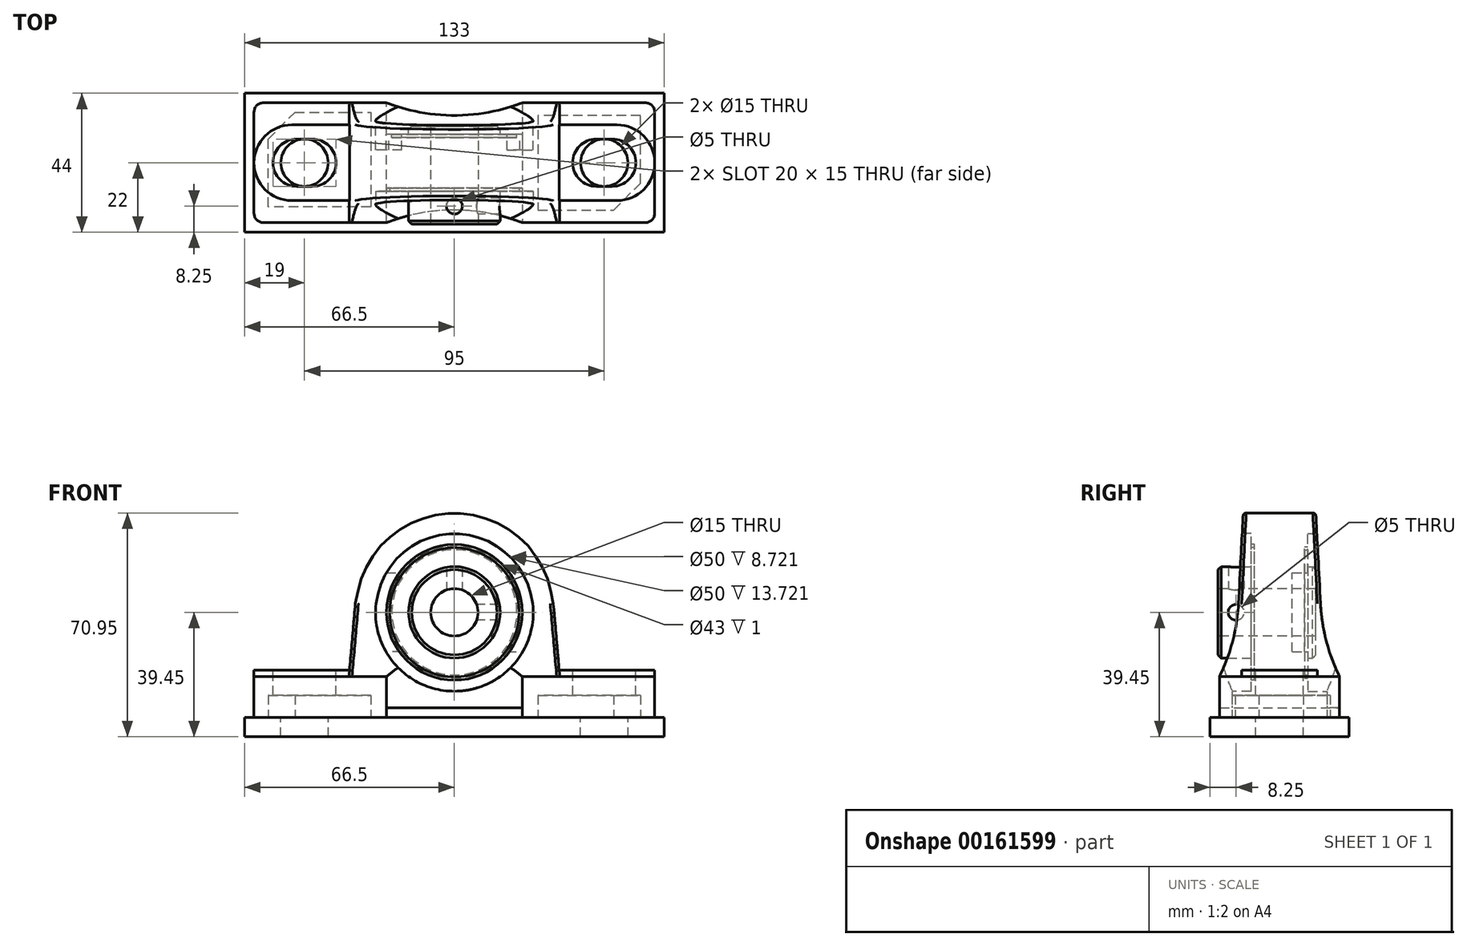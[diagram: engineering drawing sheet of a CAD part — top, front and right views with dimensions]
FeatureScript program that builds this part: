
annotation { "Feature Type Name" : "Feature", "Feature Type Description" : "" }
export const myFeature = defineFeature(function(context is Context, id is Id, definition is map)
    precondition{}
    {
        {
            var Q0;
            Q0=qCreatedBy(makeId("Front.planeOp"),FACE);
            var sketch = newSketch(context, id + "F0", { "sketchPlane" : qUnion([Q0])});
            skLineSegment(sketch, "E0", {"start": v(-63.5, 0) * mm, "end": v(0, 0) * mm});
            skLineSegment(sketch, "E1", {"start": v(-63.5, 0) * mm, "end": v(-63.5, 13) * mm});
            skLineSegment(sketch, "E2", {"start": v(-63.5, 13) * mm, "end": v(-33.4, 13) * mm});
            skCircle(sketch, "E3", {"center": v(0, 33.3) * mm, "radius": 31.5 * mm});
            skLineSegment(sketch, "E4", {"start": v(-31.38, 36.05) * mm, "end": v(-33.4, 13) * mm});
            skPoint(sketch, "E5", {"position": v(0, 64.8) * mm});
            skLineSegment(sketch, "E6.MirrorCS", {"start": v(63.5, 0) * mm, "end": v(0, 0) * mm});
            skLineSegment(sketch, "E7.MirrorCS", {"start": v(63.5, 0) * mm, "end": v(63.5, 13) * mm});
            skLineSegment(sketch, "E8.MirrorCS", {"start": v(63.5, 13) * mm, "end": v(33.4, 13) * mm});
            skLineSegment(sketch, "E9.MirrorCS", {"start": v(31.38, 36.05) * mm, "end": v(33.4, 13) * mm});
            skSolve(sketch);
        }
        {
            var Q0;
            Q0 = qSketchRegion(id + "F0", true);
            extrude(context, id + "F1", {"entities" : qUnion([Q0]), "endBound" : BoundingType.SYMMETRIC, "depth" : 38 * mm});
        }
        {
            var Q0;
            Q0=makeQuery(id+"F1.opExtrude","SWEPT_FACE",FACE,{"disambiguationData":[OSD([sQuery(id+"F0.wireOp",EDGE,"E7.MirrorCS")])]});
            var sketch = newSketch(context, id + "F2", { "sketchPlane" : qUnion([Q0])});
            skLineSegment(sketch, "E10", {"start": v(-19, 64.8) * mm, "end": v(-11.5, 64.8) * mm});
            skLineSegment(sketch, "E11", {"start": v(-11.5, 64.8) * mm, "end": v(-13, 36.05) * mm});
            skArc(sketch, "E12", {"start": v(-13, 36.05) * mm, "mid": v(-14.83, 24.22) * mm, "end": v(-19, 13) * mm});
            skLineSegment(sketch, "E13", {"start": v(-19, 13) * mm, "end": v(-19, 64.8) * mm});
            skLineSegment(sketch, "E14.MirrorCS", {"start": v(19, 64.8) * mm, "end": v(11.5, 64.8) * mm});
            skLineSegment(sketch, "E15.MirrorCS", {"start": v(11.5, 64.8) * mm, "end": v(13, 36.05) * mm});
            skArc(sketch, "E16.MirrorCS", {"start": v(13, 36.05) * mm, "mid": v(14.83, 24.22) * mm, "end": v(19, 13) * mm});
            skLineSegment(sketch, "E17.MirrorCS", {"start": v(19, 13) * mm, "end": v(19, 64.8) * mm});
            skSolve(sketch);
        }
        {
            var Q0;
            Q0 = qSketchRegion(id + "F2", true);
            var Q1;
            Q1=makeQuery(id+"F1.opExtrude","SWEPT_FACE",FACE,{"disambiguationData":[OSD([sQuery(id+"F0.wireOp",EDGE,"E1")])]});
            extrude(context, id + "F3", {"entities" : qUnion([Q0]), "operationType" : NewBodyOperationType.REMOVE, "endBound" : BoundingType.UP_TO_SURFACE, "oppositeDirection" : true, "endBoundEntityFace" : qUnion([Q1]), "depth" : 106 * mm});
        }
        {
            var Q0;
            Q0=makeQuery(id+"F1.opExtrude","SWEPT_FACE",FACE,{"disambiguationData":[OSD([sQuery(id+"F0.wireOp",EDGE,"E0"),sQuery(id+"F0.wireOp",EDGE,"E6.MirrorCS")])]});
            var sketch = newSketch(context, id + "F4", { "sketchPlane" : qUnion([Q0])});
            skArc(sketch, "E18", {"start": v(-21.5, 19) * mm, "mid": v(0, 15) * mm, "end": v(21.5, 19) * mm});
            skPoint(sketch, "E19", {"position": v(0, 15) * mm});
            skLineSegment(sketch, "E20", {"start": v(-21.5, 19) * mm, "end": v(21.5, 19) * mm});
            skArc(sketch, "E21.MirrorCS", {"start": v(-21.5, -19) * mm, "mid": v(0, -15) * mm, "end": v(21.5, -19) * mm});
            skLineSegment(sketch, "E22.MirrorCS", {"start": v(-21.5, -19) * mm, "end": v(21.5, -19) * mm});
            skPoint(sketch, "E23.MirrorP", {"position": v(0, -15) * mm});
            skSolve(sketch);
        }
        {
            var Q0;
            Q0 = qSketchRegion(id + "F4", true);
            extrude(context, id + "F5", {"entities" : qUnion([Q0]), "operationType" : NewBodyOperationType.REMOVE, "endBound" : BoundingType.UP_TO_NEXT, "oppositeDirection" : true, "depth" : 25 * mm});
        }
        {
            var Q0;
            {var subQ0=sQuery(id+"F0.wireOp",EDGE,"E4");var subQ1=sQuery(id+"F0.wireOp",EDGE,"E2");var subQ2=sQuery(id+"F0.wireOp",EDGE,"E1");var subQ3=sQuery(id+"F0.wireOp",EDGE,"E6.MirrorCS");var subQ4=sQuery(id+"F0.wireOp",EDGE,"E0");Q0=makeQuery(id+"F5.boolean.opBoolean","SPLIT",FACE,{"disambiguationData":[TD([makeQuery(id+"F1.opExtrude","SWEPT_FACE",FACE,{"disambiguationData":[OSD([subQ2])]})])],"derivedFrom":makeQuery(id+"F1.opExtrude","CAP_FACE",FACE,{"disambiguationData":[OSD([subQ4,subQ2,subQ1,sQuery(id+"F0.wireOp",EDGE,"E3"),subQ0,subQ3,sQuery(id+"F0.wireOp",EDGE,"E7.MirrorCS"),sQuery(id+"F0.wireOp",EDGE,"E8.MirrorCS"),sQuery(id+"F0.wireOp",EDGE,"E9.MirrorCS")])],"isStart":false})});}
            var sketch = newSketch(context, id + "F6", { "sketchPlane" : qUnion([Q0])});
            skCircle(sketch, "E24", {"center": v(0, 33.3) * mm, "radius": 25 * mm});
            skSolve(sketch);
        }
        {
            var Q0;
            Q0 = qSketchRegion(id + "F6", true);
            extrude(context, id + "F7", {"entities" : qUnion([Q0]), "operationType" : NewBodyOperationType.REMOVE, "oppositeDirection" : true, "depth" : 10 * mm});
        }
        {
            var Q0;
            {var subQ0=sQuery(id+"F0.wireOp",EDGE,"E7.MirrorCS");var subQ1=sQuery(id+"F0.wireOp",EDGE,"E9.MirrorCS");var subQ2=sQuery(id+"F0.wireOp",EDGE,"E8.MirrorCS");var subQ3=sQuery(id+"F0.wireOp",EDGE,"E6.MirrorCS");var subQ4=sQuery(id+"F0.wireOp",EDGE,"E0");Q0=makeQuery(id+"F5.boolean.opBoolean","SPLIT",FACE,{"disambiguationData":[TD([makeQuery(id+"F1.opExtrude","SWEPT_FACE",FACE,{"disambiguationData":[OSD([subQ0])]})])],"derivedFrom":makeQuery(id+"F1.opExtrude","CAP_FACE",FACE,{"disambiguationData":[OSD([subQ4,sQuery(id+"F0.wireOp",EDGE,"E1"),sQuery(id+"F0.wireOp",EDGE,"E2"),sQuery(id+"F0.wireOp",EDGE,"E3"),sQuery(id+"F0.wireOp",EDGE,"E4"),subQ3,subQ0,subQ2,subQ1])],"isStart":true})});}
            var sketch = newSketch(context, id + "F8", { "sketchPlane" : qUnion([Q0])});
            skCircle(sketch, "E25", {"center": v(0, 33.3) * mm, "radius": 25 * mm});
            skSolve(sketch);
        }
        {
            var Q0;
            Q0 = qSketchRegion(id + "F8", true);
            extrude(context, id + "F9", {"entities" : qUnion([Q0]), "operationType" : NewBodyOperationType.REMOVE, "oppositeDirection" : true, "depth" : 10 * mm});
        }
        {
            var Q0;
            Q0=makeQuery(id+"F7.boolean.opBoolean","COPY",FACE,{"derivedFrom":makeQuery(id+"F7.opExtrude","CAP_FACE",FACE,{"disambiguationData":[OSD([sQuery(id+"F6.wireOp",EDGE,"E24")])],"isStart":false})});
            var sketch = newSketch(context, id + "F10", { "sketchPlane" : qUnion([Q0])});
            skCircle(sketch, "E26", {"center": v(0, 33.3) * mm, "radius": 21.5 * mm});
            skCircle(sketch, "E27", {"center": v(0, 33.3) * mm, "radius": 20.5 * mm});
            skSolve(sketch);
        }
        {
            var Q0;
            Q0 = qSketchRegion(id + "F10", true);
            extrude(context, id + "F11", {"entities" : qUnion([Q0]), "operationType" : NewBodyOperationType.REMOVE, "oppositeDirection" : true, "depth" : 1 * mm});
        }
        {
            var Q0;
            Q0=qCreatedBy(makeId("Front.planeOp"),FACE);
            cPlane(context, id + "F12", {"entities" : qUnion([Q0]), "cplaneType" : CPlaneType.OFFSET, "offset" : 4 * mm, "width" : 150 * mm, "height" : 150 * mm});
        }
        {
            var Q0;
            Q0=qCreatedBy(id+"F12.planeOp",FACE);
            var sketch = newSketch(context, id + "F13", { "sketchPlane" : qUnion([Q0])});
            skCircle(sketch, "E28", {"center": v(0, 33.3) * mm, "radius": 14.5 * mm});
            skSolve(sketch);
        }
        {
            var Q0;
            Q0 = qSketchRegion(id + "F13", true);
            extrude(context, id + "F14", {"entities" : qUnion([Q0]), "operationType" : NewBodyOperationType.ADD, "endBound" : BoundingType.SYMMETRIC, "depth" : 31 * mm});
        }
        {
            var Q0;
            Q0=makeQuery(id+"F14.opExtrude","CAP_FACE",FACE,{"disambiguationData":[OSD([sQuery(id+"F13.wireOp",EDGE,"E28")])],"isStart":false});
            var sketch = newSketch(context, id + "F15", { "sketchPlane" : qUnion([Q0])});
            skCircle(sketch, "E29", {"center": v(0, 33.3) * mm, "radius": 7.5 * mm});
            skSolve(sketch);
        }
        {
            var Q0;
            Q0 = qSketchRegion(id + "F15", true);
            extrude(context, id + "F16", {"entities" : qUnion([Q0]), "operationType" : NewBodyOperationType.REMOVE, "endBound" : BoundingType.UP_TO_NEXT, "oppositeDirection" : true, "depth" : 25 * mm});
        }
        {
            var Q0;
            Q0=makeQuery(id+"F9.boolean.opBoolean","COPY",FACE,{"derivedFrom":makeQuery(id+"F9.opExtrude","CAP_FACE",FACE,{"disambiguationData":[OSD([sQuery(id+"F8.wireOp",EDGE,"E25")])],"isStart":false})});
            var sketch = newSketch(context, id + "F17", { "sketchPlane" : qUnion([Q0])});
            skArc(sketch, "E30", {"start": v(-21.65, 45.8) * mm, "mid": v(-25, 33.3) * mm, "end": v(-21.65, 20.8) * mm});
            skArc(sketch, "E31", {"start": v(-16.65, 45.8) * mm, "mid": v(-20.82, 33.3) * mm, "end": v(-16.65, 20.8) * mm});
            skLineSegment(sketch, "E32", {"start": v(-21.65, 45.8) * mm, "end": v(-16.65, 45.8) * mm});
            skLineSegment(sketch, "E33", {"start": v(-16.65, 20.8) * mm, "end": v(-21.65, 20.8) * mm});
            skPoint(sketch, "E34", {"position": v(-20.82, 33.3) * mm});
            skArc(sketch, "E35.MirrorCS", {"start": v(16.65, 45.8) * mm, "mid": v(20.82, 33.3) * mm, "end": v(16.65, 20.8) * mm});
            skArc(sketch, "E36.MirrorCS", {"start": v(21.65, 45.8) * mm, "mid": v(25, 33.3) * mm, "end": v(21.65, 20.8) * mm});
            skPoint(sketch, "E37.MirrorP", {"position": v(20.82, 33.3) * mm});
            skLineSegment(sketch, "E38.MirrorCS", {"start": v(16.65, 20.8) * mm, "end": v(21.65, 20.8) * mm});
            skLineSegment(sketch, "E39.MirrorCS", {"start": v(21.65, 45.8) * mm, "end": v(16.65, 45.8) * mm});
            skSolve(sketch);
        }
        {
            var Q0;
            Q0 = qSketchRegion(id + "F17", true);
            extrude(context, id + "F18", {"entities" : qUnion([Q0]), "operationType" : NewBodyOperationType.REMOVE, "oppositeDirection" : true, "depth" : 5 * mm});
        }
        {
            var Q0;
            Q0=makeQuery(id+"F9.boolean.opBoolean","COPY",FACE,{"derivedFrom":makeQuery(id+"F9.opExtrude","CAP_FACE",FACE,{"disambiguationData":[OSD([sQuery(id+"F8.wireOp",EDGE,"E25")])],"isStart":false})});
            var sketch = newSketch(context, id + "F19", { "sketchPlane" : qUnion([Q0])});
            skCircle(sketch, "E40", {"center": v(0, 33.3) * mm, "radius": 20.82 * mm});
            skCircle(sketch, "E41", {"center": v(0, 33.3) * mm, "radius": 19.82 * mm});
            skSolve(sketch);
        }
        {
            var Q0;
            Q0 = qSketchRegion(id + "F19", true);
            extrude(context, id + "F20", {"entities" : qUnion([Q0]), "operationType" : NewBodyOperationType.REMOVE, "oppositeDirection" : true, "depth" : 1 * mm});
        }
        {
            var Q0;
            Q0=makeQuery(id+"F1.opExtrude","SWEPT_FACE",FACE,{"disambiguationData":[OSD([sQuery(id+"F0.wireOp",EDGE,"E0"),sQuery(id+"F0.wireOp",EDGE,"E6.MirrorCS")])]});
            var sketch = newSketch(context, id + "F21", { "sketchPlane" : qUnion([Q0])});
            skLineSegment(sketch, "E42", {"start": v(-21.5, 19) * mm, "end": v(-21.5, -19) * mm});
            skLineSegment(sketch, "E43", {"start": v(-21.5, -19) * mm, "end": v(21.5, -19) * mm});
            skLineSegment(sketch, "E44", {"start": v(21.5, -19) * mm, "end": v(21.5, 19) * mm});
            skLineSegment(sketch, "E45", {"start": v(21.5, 19) * mm, "end": v(-21.5, 19) * mm});
            skSolve(sketch);
        }
        {
            var Q0;
            Q0 = qSketchRegion(id + "F21", true);
            extrude(context, id + "F22", {"entities" : qUnion([Q0]), "operationType" : NewBodyOperationType.REMOVE, "oppositeDirection" : true, "depth" : 3 * mm});
        }
        {
            var Q0;
            {var subQ3=sQuery(id+"F0.wireOp",EDGE,"E6.MirrorCS");var subQ7=sQuery(id+"F0.wireOp",EDGE,"E1");var subQ8=sQuery(id+"F0.wireOp",EDGE,"E0");Q0=makeQuery(id+"F22.boolean.opBoolean","SPLIT",FACE,{"disambiguationData":[TD([makeQuery(id+"F1.opExtrude","SWEPT_FACE",FACE,{"disambiguationData":[OSD([subQ7])]})])],"derivedFrom":makeQuery(id+"F1.opExtrude","SWEPT_FACE",FACE,{"disambiguationData":[OSD([subQ8,subQ3])]})});}
            var sketch = newSketch(context, id + "F23", { "sketchPlane" : qUnion([Q0])});
            skLineSegment(sketch, "E46", {"start": v(26.5, 15) * mm, "end": v(50.51, 15) * mm});
            skLineSegment(sketch, "E47", {"start": v(50.51, 15) * mm, "end": v(59, 6.51) * mm});
            skLineSegment(sketch, "E48", {"start": v(59, 6.51) * mm, "end": v(59, -15) * mm});
            skLineSegment(sketch, "E49", {"start": v(59, -15) * mm, "end": v(26.5, -15) * mm});
            skLineSegment(sketch, "E50", {"start": v(26.5, -15) * mm, "end": v(26.5, 15) * mm});
            skPoint(sketch, "E51", {"position": v(26.5, 0) * mm});
            skLineSegment(sketch, "E52", {"start": v(-59, -7.51) * mm, "end": v(-50.51, -16) * mm});
            skLineSegment(sketch, "E53", {"start": v(-50.51, -16) * mm, "end": v(-26.5, -16) * mm});
            skLineSegment(sketch, "E54", {"start": v(-26.5, -16) * mm, "end": v(-26.5, 14) * mm});
            skLineSegment(sketch, "E55", {"start": v(-26.5, 14) * mm, "end": v(-59, 14) * mm});
            skLineSegment(sketch, "E56", {"start": v(-59, 14) * mm, "end": v(-59, -7.51) * mm});
            skSolve(sketch);
        }
        {
            var Q0;
            Q0 = qSketchRegion(id + "F23", true);
            extrude(context, id + "F24", {"entities" : qUnion([Q0]), "operationType" : NewBodyOperationType.REMOVE, "oppositeDirection" : true, "depth" : 7 * mm});
        }
        {
            var Q0;
            Q0=makeQuery(id+"F1.opExtrude","SWEPT_FACE",FACE,{"disambiguationData":[OSD([sQuery(id+"F0.wireOp",EDGE,"E2")])]});
            var sketch = newSketch(context, id + "F25", { "sketchPlane" : qUnion([Q0])});
            skLineSegment(sketch, "E57", {"start": v(31.38, 12) * mm, "end": v(51.5, 12) * mm});
            skLineSegment(sketch, "E58", {"start": v(31.38, 12) * mm, "end": v(31.38, -12) * mm});
            skLineSegment(sketch, "E59", {"start": v(31.38, -12) * mm, "end": v(51.5, -12) * mm});
            skArc(sketch, "E60", {"start": v(51.5, 12) * mm, "mid": v(63.5, 0) * mm, "end": v(51.5, -12) * mm});
            skArc(sketch, "E61.MirrorCS", {"start": v(-51.5, 12) * mm, "mid": v(-63.5, 0) * mm, "end": v(-51.5, -12) * mm});
            skLineSegment(sketch, "E62.MirrorCS", {"start": v(-31.38, -12) * mm, "end": v(-51.5, -12) * mm});
            skLineSegment(sketch, "E63.MirrorCS", {"start": v(-31.38, 12) * mm, "end": v(-31.38, -12) * mm});
            skLineSegment(sketch, "E64.MirrorCS", {"start": v(-31.38, 12) * mm, "end": v(-51.5, 12) * mm});
            skSolve(sketch);
        }
        {
            var Q0;
            Q0 = qSketchRegion(id + "F25", true);
            extrude(context, id + "F26", {"entities" : qUnion([Q0]), "operationType" : NewBodyOperationType.ADD, "depth" : 2 * mm});
        }
        {
            var Q0;
            Q0=makeQuery(id+"F26.opExtrude","CAP_FACE",FACE,{"disambiguationData":[OSD([sQuery(id+"F25.wireOp",EDGE,"E61.MirrorCS"),sQuery(id+"F25.wireOp",EDGE,"E62.MirrorCS"),sQuery(id+"F25.wireOp",EDGE,"E63.MirrorCS"),sQuery(id+"F25.wireOp",EDGE,"E64.MirrorCS")])],"isStart":false});
            var sketch = newSketch(context, id + "F27", { "sketchPlane" : qUnion([Q0])});
            skLineSegment(sketch, "E65.bottom", {"start": v(-50, 7.5) * mm, "end": v(-45, 7.5) * mm});
            skLineSegment(sketch, "E65.top", {"start": v(-50, -7.5) * mm, "end": v(-45, -7.5) * mm});
            skLineSegment(sketch, "E65.left", {"start": v(-50, 7.5) * mm, "end": v(-50, -7.5) * mm, "construction": true});
            skLineSegment(sketch, "E65.right", {"start": v(-45, 7.5) * mm, "end": v(-45, -7.5) * mm, "construction": true});
            skPoint(sketch, "E65.middle", {"position": v(-47.5, 0) * mm});
            skArc(sketch, "E66", {"start": v(-50, 7.5) * mm, "mid": v(-57.5, 0) * mm, "end": v(-50, -7.5) * mm});
            skArc(sketch, "E67", {"start": v(-45, 7.5) * mm, "mid": v(-37.5, 0) * mm, "end": v(-45, -7.5) * mm});
            skPoint(sketch, "E68", {"position": v(-37.5, 0) * mm});
            skPoint(sketch, "E69", {"position": v(-57.5, 0) * mm});
            skPoint(sketch, "E70.MirrorP", {"position": v(47.5, 0) * mm});
            skPoint(sketch, "E71.MirrorP", {"position": v(37.5, 0) * mm});
            skPoint(sketch, "E72.MirrorP", {"position": v(57.5, 0) * mm});
            skLineSegment(sketch, "E73.MirrorCS", {"start": v(50, 7.5) * mm, "end": v(45, 7.5) * mm});
            skLineSegment(sketch, "E74.MirrorCS", {"start": v(50, -7.5) * mm, "end": v(45, -7.5) * mm});
            skLineSegment(sketch, "E75.MirrorCS", {"start": v(50, 7.5) * mm, "end": v(50, -7.5) * mm, "construction": true});
            skLineSegment(sketch, "E76.MirrorCS", {"start": v(45, 7.5) * mm, "end": v(45, -7.5) * mm, "construction": true});
            skArc(sketch, "E77.MirrorCS", {"start": v(50, 7.5) * mm, "mid": v(57.5, 0) * mm, "end": v(50, -7.5) * mm});
            skArc(sketch, "E78.MirrorCS", {"start": v(45, 7.5) * mm, "mid": v(37.5, 0) * mm, "end": v(45, -7.5) * mm});
            skSolve(sketch);
        }
        {
            var Q0;
            Q0 = qSketchRegion(id + "F27", true);
            extrude(context, id + "F28", {"entities" : qUnion([Q0]), "operationType" : NewBodyOperationType.REMOVE, "endBound" : BoundingType.UP_TO_NEXT, "oppositeDirection" : true, "depth" : 25 * mm});
        }
        {
            var Q0;
            Q0=makeQuery(id+"F26.opExtrude","CAP_EDGE",EDGE,{"disambiguationData":[OSD([sQuery(id+"F25.wireOp",EDGE,"E62.MirrorCS")])],"isStart":true});
            var Q1;
            Q1=makeQuery(id+"F26.opExtrude","CAP_EDGE",EDGE,{"disambiguationData":[OSD([sQuery(id+"F25.wireOp",EDGE,"E59")])],"isStart":true});
            var Q2;
            Q2=makeQuery(id+"F3.boolean.opBoolean","INTERSECT",EDGE,{"derivedFrom":[makeQuery(id+"F1.opExtrude","SWEPT_FACE",FACE,{"disambiguationData":[OSD([sQuery(id+"F0.wireOp",EDGE,"E3")])]}),makeQuery(id+"F3.opExtrude","SWEPT_FACE",FACE,{"disambiguationData":[OSD([sQuery(id+"F2.wireOp",EDGE,"E11")])]})]});
            var Q3;
            Q3=makeQuery(id+"F3.boolean.opBoolean","INTERSECT",EDGE,{"derivedFrom":[makeQuery(id+"F1.opExtrude","SWEPT_FACE",FACE,{"disambiguationData":[OSD([sQuery(id+"F0.wireOp",EDGE,"E3")])]}),makeQuery(id+"F3.opExtrude","SWEPT_FACE",FACE,{"disambiguationData":[OSD([sQuery(id+"F2.wireOp",EDGE,"E15.MirrorCS")])]})]});
            fillet(context, id + "F29", {"entities" : qUnion([Q0, Q1, Q2, Q3]), "radius" : 1 * mm, "tangentPropagation" : true, "allowEdgeOverflow" : false});
        }
        {
            var Q0;
            Q0=makeQuery(id+"F1.opExtrude","CAP_EDGE",EDGE,{"disambiguationData":[OSD([sQuery(id+"F0.wireOp",EDGE,"E1")])],"isStart":false});
            var Q1;
            Q1=makeQuery(id+"F1.opExtrude","CAP_EDGE",EDGE,{"disambiguationData":[OSD([sQuery(id+"F0.wireOp",EDGE,"E1")])],"isStart":true});
            var Q2;
            Q2=makeQuery(id+"F1.opExtrude","CAP_EDGE",EDGE,{"disambiguationData":[OSD([sQuery(id+"F0.wireOp",EDGE,"E7.MirrorCS")])],"isStart":false});
            var Q3;
            Q3=makeQuery(id+"F1.opExtrude","CAP_EDGE",EDGE,{"disambiguationData":[OSD([sQuery(id+"F0.wireOp",EDGE,"E7.MirrorCS")])],"isStart":true});
            fillet(context, id + "F30", {"entities" : qUnion([Q0, Q1, Q2, Q3]), "radius" : 3 * mm, "tangentPropagation" : true, "allowEdgeOverflow" : false});
        }
        {
            var Q0;
            Q0=makeQuery(id+"F14.opExtrude","CAP_EDGE",EDGE,{"disambiguationData":[OSD([sQuery(id+"F13.wireOp",EDGE,"E28")])],"isStart":false});
            var Q1;
            Q1=makeQuery(id+"F14.opExtrude","CAP_EDGE",EDGE,{"disambiguationData":[OSD([sQuery(id+"F13.wireOp",EDGE,"E28")])],"isStart":true});
            chamfer(context, id + "F31", {"entities" : qUnion([Q0, Q1]), "width" : 1 * mm, "tangentPropagation" : true});
        }
        {
            var Q0;
            Q0=qCreatedBy(makeId("Top.planeOp"),FACE);
            cPlane(context, id + "F32", {"entities" : qUnion([Q0]), "cplaneType" : CPlaneType.OFFSET, "offset" : 33.3 * mm, "width" : 150 * mm, "height" : 150 * mm});
        }
        {
            var Q0;
            Q0=qCreatedBy(id+"F32.planeOp",FACE);
            var sketch = newSketch(context, id + "F33", { "sketchPlane" : qUnion([Q0])});
            skCircle(sketch, "E79", {"center": v(0, -13.75) * mm, "radius": 2.5 * mm});
            skLineSegment(sketch, "E80.0", {"start": v(-14.5, -9) * mm, "end": v(14.5, -9) * mm, "construction": true});
            skLineSegment(sketch, "E81.0", {"start": v(-14.5, -18.5) * mm, "end": v(14.5, -18.5) * mm, "construction": true});
            skLineSegment(sketch, "E82", {"start": v(0, -18.5) * mm, "end": v(0, -9) * mm, "construction": true});
            skSolve(sketch);
        }
        {
            var Q0;
            Q0 = qSketchRegion(id + "F33", true);
            extrude(context, id + "F34", {"entities" : qUnion([Q0]), "operationType" : NewBodyOperationType.REMOVE, "depth" : 15 * mm});
        }
        {
            var Q0;
            Q0=qCreatedBy(makeId("Right.planeOp"),FACE);
            var sketch = newSketch(context, id + "F35", { "sketchPlane" : qUnion([Q0])});
            skLineSegment(sketch, "E83.0", {"start": v(-9, 47.8) * mm, "end": v(-9, 18.8) * mm, "construction": true});
            skLineSegment(sketch, "E84.0", {"start": v(-18.5, 47.8) * mm, "end": v(-18.5, 18.8) * mm, "construction": true});
            skLineSegment(sketch, "E85", {"start": v(-18.5, 33.3) * mm, "end": v(-9, 33.3) * mm, "construction": true});
            skPoint(sketch, "E86", {"position": v(-13.75, 33.3) * mm});
            skCircle(sketch, "E87", {"center": v(-13.75, 33.3) * mm, "radius": 2.5 * mm});
            skSolve(sketch);
        }
        {
            var Q0;
            Q0 = qSketchRegion(id + "F35", true);
            extrude(context, id + "F36", {"entities" : qUnion([Q0]), "operationType" : NewBodyOperationType.REMOVE, "depth" : 15 * mm});
        }
        {
            var Q0;
            {var subQ3=sQuery(id+"F0.wireOp",EDGE,"E6.MirrorCS");var subQ7=sQuery(id+"F0.wireOp",EDGE,"E1");var subQ8=sQuery(id+"F0.wireOp",EDGE,"E0");Q0=makeQuery(id+"F22.boolean.opBoolean","SPLIT",FACE,{"disambiguationData":[TD([makeQuery(id+"F1.opExtrude","SWEPT_FACE",FACE,{"disambiguationData":[OSD([subQ7])]})])],"derivedFrom":makeQuery(id+"F1.opExtrude","SWEPT_FACE",FACE,{"disambiguationData":[OSD([subQ8,subQ3])]})});}
            var sketch = newSketch(context, id + "F37", { "sketchPlane" : qUnion([Q0])});
            skLineSegment(sketch, "E88.bottom", {"start": v(66.5, 22) * mm, "end": v(-66.5, 22) * mm});
            skLineSegment(sketch, "E88.top", {"start": v(66.5, -22) * mm, "end": v(-66.5, -22) * mm});
            skLineSegment(sketch, "E88.left", {"start": v(66.5, 22) * mm, "end": v(66.5, -22) * mm});
            skLineSegment(sketch, "E88.right", {"start": v(-66.5, 22) * mm, "end": v(-66.5, -22) * mm});
            skPoint(sketch, "E88.middle", {"position": v(0, 0) * mm});
            skSolve(sketch);
        }
        {
            var Q0;
            Q0 = qSketchRegion(id + "F37", true);
            extrude(context, id + "F38", {"entities" : qUnion([Q0]), "depth" : 6.15 * mm});
        }
        {
            var Q0;
            Q0=makeQuery(id+"F38.opExtrude","CAP_FACE",FACE,{"disambiguationData":[OSD([sQuery(id+"F37.wireOp",EDGE,"E88.bottom"),sQuery(id+"F37.wireOp",EDGE,"E88.top"),sQuery(id+"F37.wireOp",EDGE,"E88.left"),sQuery(id+"F37.wireOp",EDGE,"E88.right")])],"isStart":true});
            var sketch = newSketch(context, id + "F39", { "sketchPlane" : qUnion([Q0])});
            skCircle(sketch, "E89", {"center": v(-47.5, 0) * mm, "radius": 7.5 * mm});
            skPoint(sketch, "E90.0", {"position": v(-47.5, -7.5) * mm});
            skCircle(sketch, "E91.MirrorC", {"center": v(47.5, 0) * mm, "radius": 7.5 * mm});
            skSolve(sketch);
        }
        {
            var Q0;
            Q0 = qSketchRegion(id + "F39", true);
            extrude(context, id + "F40", {"entities" : qUnion([Q0]), "operationType" : NewBodyOperationType.REMOVE, "endBound" : BoundingType.UP_TO_NEXT, "oppositeDirection" : true, "depth" : 25 * mm});
        }
    });
